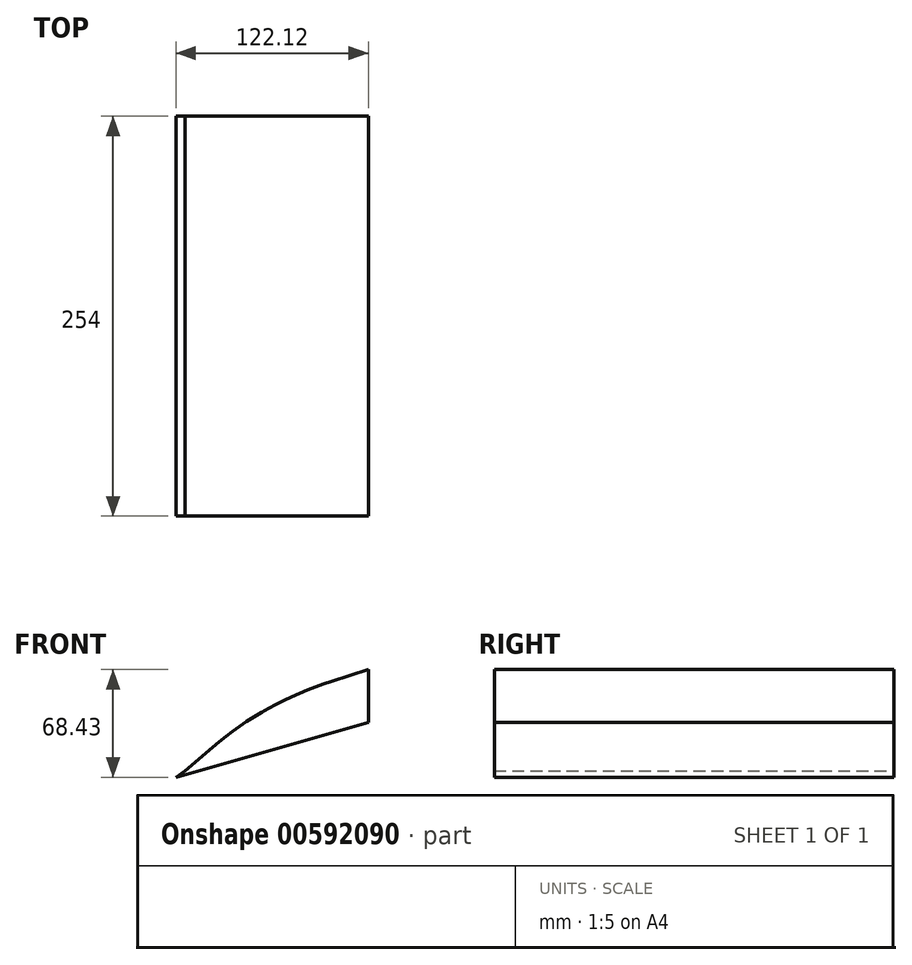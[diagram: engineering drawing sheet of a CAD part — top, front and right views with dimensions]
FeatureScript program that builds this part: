
annotation { "Feature Type Name" : "Feature", "Feature Type Description" : "" }
export const myFeature = defineFeature(function(context is Context, id is Id, definition is map)
    precondition{}
    {
        {
            var Q0;
            Q0=qCreatedBy(makeId("Front.planeOp"),FACE);
            var sketch = newSketch(context, id + "F0", { "sketchPlane" : qUnion([Q0])});
            skLineSegment(sketch, "E0", {"start": v(1599.44, 450.5) * mm, "end": v(1599.44, 416.96) * mm});
            skLineSegment(sketch, "E1", {"start": v(1599.44, 450.5) * mm, "end": v(1576.08, 443.08) * mm});
            skLineSegment(sketch, "E2", {"start": v(1500.52, 401.12) * mm, "end": v(1483.14, 386.3) * mm});
            skLineSegment(sketch, "E3", {"start": v(1599.44, 416.96) * mm, "end": v(1477.32, 382.07) * mm});
            skLineSegment(sketch, "E4", {"start": v(1483.14, 386.3) * mm, "end": v(1477.32, 382.07) * mm});
            skPoint(sketch, "E5.visualSharp", {"position": v(1534.06, 429.73) * mm});
            skArc(sketch, "E5.filletArc", {"start": v(1576.08, 443.08) * mm, "mid": v(1536.2, 425.88) * mm, "end": v(1500.52, 401.12) * mm});
            skSolve(sketch);
        }
        {
            var Q0;
            Q0 = qSketchRegion(id + "F0", true);
            extrude(context, id + "F1", {"entities" : qUnion([Q0]), "depth" : 254 * mm, "offsetDistance" : 25.4 * mm});
        }
    });
